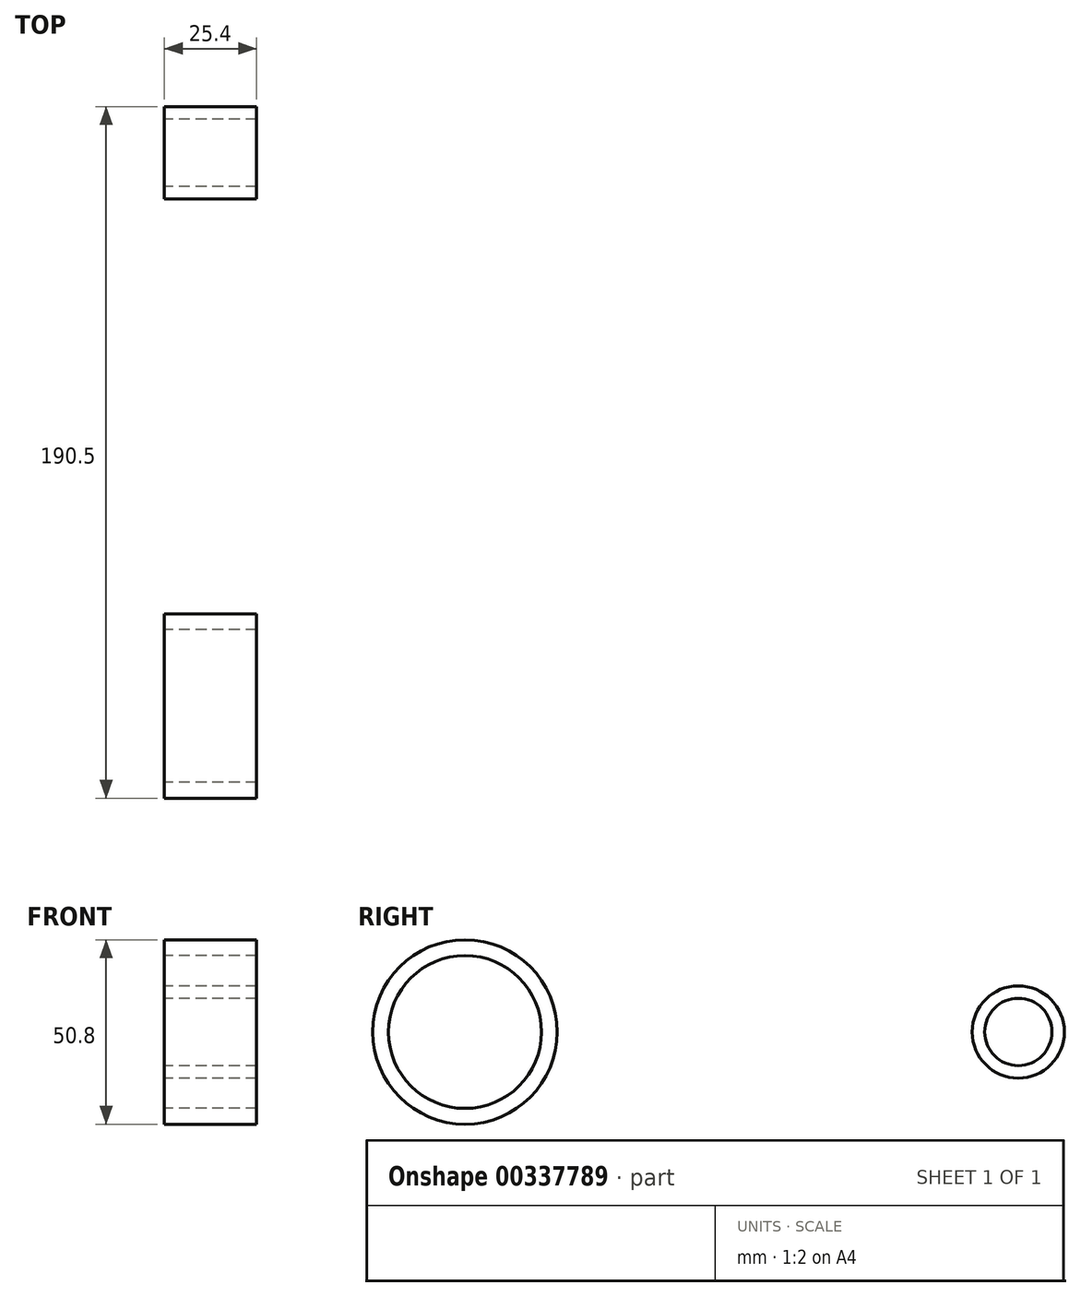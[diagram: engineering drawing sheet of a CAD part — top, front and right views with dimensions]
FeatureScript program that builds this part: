
annotation { "Feature Type Name" : "Feature", "Feature Type Description" : "" }
export const myFeature = defineFeature(function(context is Context, id is Id, definition is map)
    precondition{}
    {
        {
            var Q0;
            Q0=qCreatedBy(makeId("Right.planeOp"),FACE);
            var sketch = newSketch(context, id + "F0", { "sketchPlane" : qUnion([Q0])});
            skCircle(sketch, "E0", {"center": v(0, 0) * mm, "radius": 25.4 * mm});
            skCircle(sketch, "E1", {"center": v(152.4, 0) * mm, "radius": 12.7 * mm});
            skLineSegment(sketch, "E2", {"start": v(0, 0) * mm, "end": v(152.4, 0) * mm, "construction": true});
            skLineSegment(sketch, "E3", {"start": v(0, 25.4) * mm, "end": v(152.4, 12.74) * mm});
            skLineSegment(sketch, "E4.MirrorCS", {"start": v(0, -25.4) * mm, "end": v(152.4, -12.74) * mm});
            skCircle(sketch, "E5", {"center": v(0, 0) * mm, "radius": 21.06 * mm});
            skCircle(sketch, "E6", {"center": v(152.4, 0) * mm, "radius": 9.27 * mm});
            skSolve(sketch);
        }
        {
            var Q0;
            Q0 = qSketchRegion(id + "F0", true);
            extrude(context, id + "F1", {"entities" : qUnion([Q0]), "depth" : 25.4 * mm});
        }
    });
